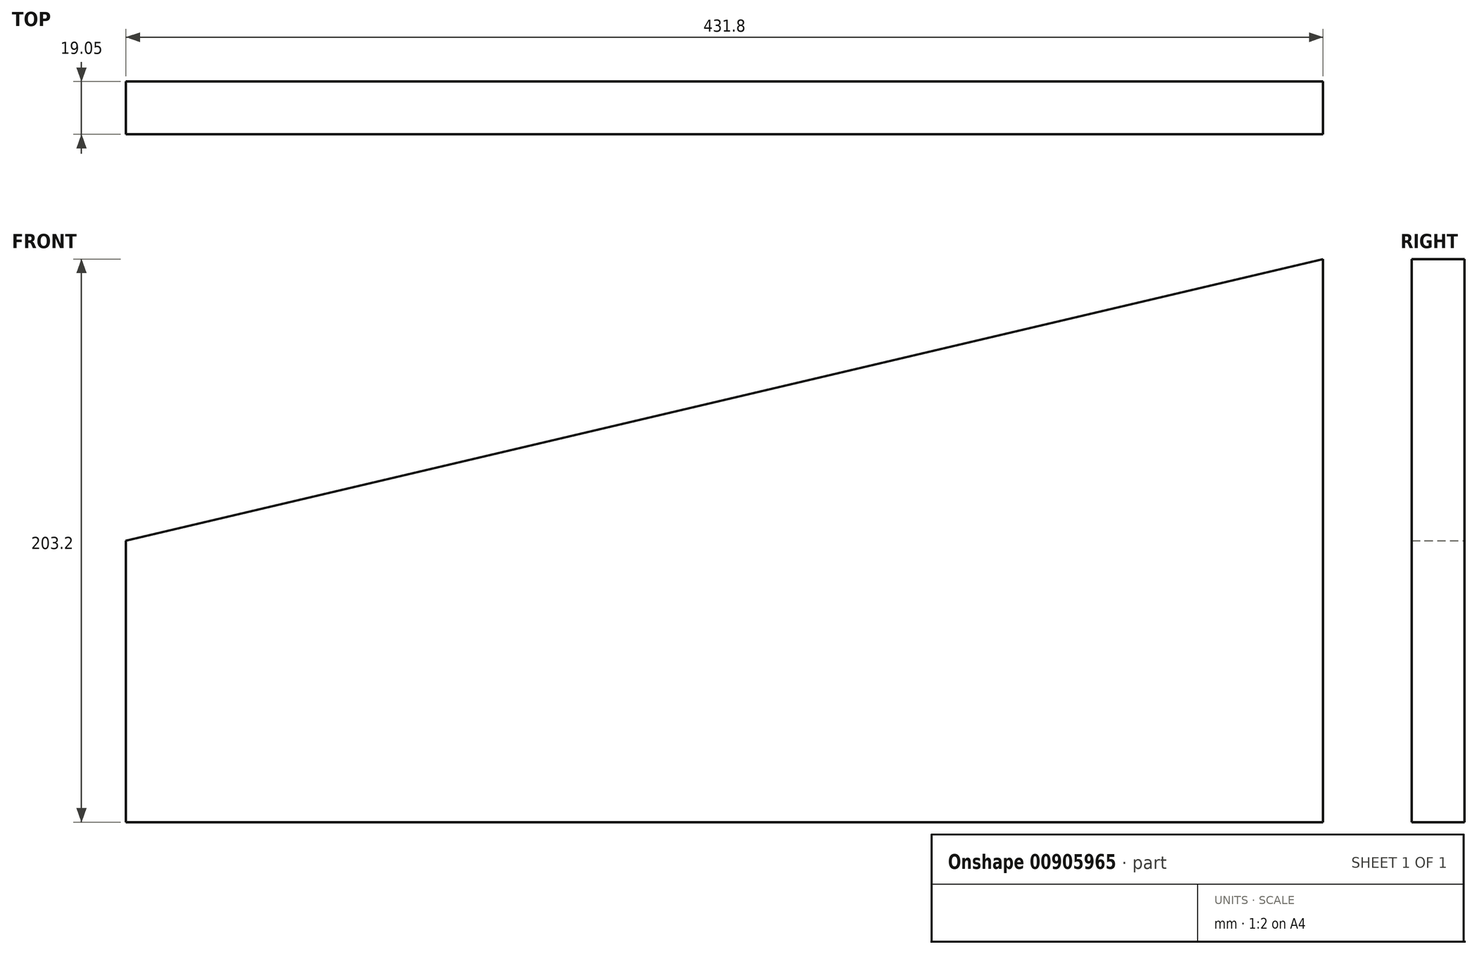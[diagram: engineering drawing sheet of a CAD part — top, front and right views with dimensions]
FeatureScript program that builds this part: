
annotation { "Feature Type Name" : "Feature", "Feature Type Description" : "" }
export const myFeature = defineFeature(function(context is Context, id is Id, definition is map)
    precondition{}
    {
        {
            var Q0;
            Q0=qCreatedBy(makeId("Front.planeOp"),FACE);
            var sketch = newSketch(context, id + "F0", { "sketchPlane" : qUnion([Q0])});
            skLineSegment(sketch, "E0", {"start": v(0, 0) * mm, "end": v(431.8, 101.6) * mm});
            skLineSegment(sketch, "E1.top", {"start": v(0, -101.6) * mm, "end": v(431.8, -101.6) * mm});
            skLineSegment(sketch, "E1.left", {"start": v(0, 0) * mm, "end": v(0, -101.6) * mm});
            skLineSegment(sketch, "E2", {"start": v(431.8, 101.6) * mm, "end": v(431.8, -101.6) * mm});
            skSolve(sketch);
        }
        {
            var Q0;
            Q0=makeQuery(id+"F0.imprint","IMPRINT",FACE,{"disambiguationData":[TD([[makeQuery(id+"F0.imprint","IMPRINT",EDGE,{"derivedFrom":sQuery(id+"F0.wireOp",EDGE,"E0")}),-1.0]])]});
            extrude(context, id + "F1", {"entities" : qUnion([Q0]), "depth" : 19.05 * mm, "offsetDistance" : 25.4 * mm});
        }
    });
